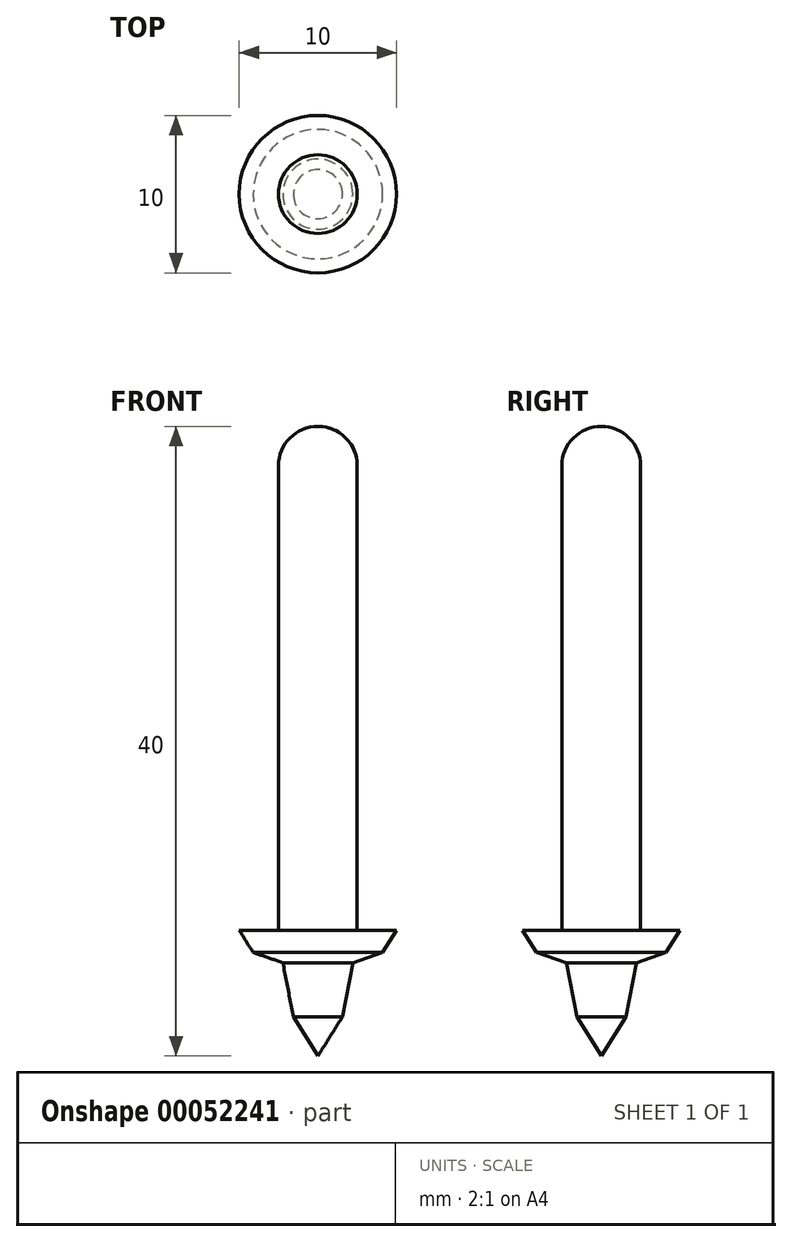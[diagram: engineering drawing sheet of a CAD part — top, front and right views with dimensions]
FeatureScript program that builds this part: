
annotation { "Feature Type Name" : "Feature", "Feature Type Description" : "" }
export const myFeature = defineFeature(function(context is Context, id is Id, definition is map)
    precondition{}
    {
        {
            var Q0;
            Q0=qCreatedBy(makeId("Front.planeOp"),FACE);
            var sketch = newSketch(context, id + "F0", { "sketchPlane" : qUnion([Q0])});
            skLineSegment(sketch, "E0", {"start": v(0, 0) * mm, "end": v(0, 40) * mm});
            skLineSegment(sketch, "E1", {"start": v(0, 8) * mm, "end": v(2.5, 8) * mm});
            skLineSegment(sketch, "E2", {"start": v(2.5, 8) * mm, "end": v(2.5, 37.5) * mm});
            skArc(sketch, "E3", {"start": v(2.5, 37.5) * mm, "mid": v(1.77, 39.27) * mm, "end": v(0, 40) * mm});
            skLineSegment(sketch, "E4", {"start": v(2.5, 37.5) * mm, "end": v(0, 37.5) * mm});
            skLineSegment(sketch, "E5", {"start": v(2.5, 8) * mm, "end": v(5, 8) * mm});
            skLineSegment(sketch, "E6", {"start": v(5, 8) * mm, "end": v(0, 0) * mm});
            skLineSegment(sketch, "E7", {"start": v(1.56, 2.5) * mm, "end": v(2.22, 5.93) * mm});
            skLineSegment(sketch, "E8", {"start": v(2.22, 5.93) * mm, "end": v(4.11, 6.58) * mm});
            skSolve(sketch);
        }
        {
            var Q0;
            {var subQ0=sQuery(id+"F0.wireOp",EDGE,"E1");Q0=makeQuery(id+"F0.imprint","IMPRINT",FACE,{"disambiguationData":[TD([[makeQuery(id+"F0.imprint","IMPRINT",EDGE,{"derivedFrom":subQ0}),1.0]])]});}
            var Q1;
            {var subQ0=sQuery(id+"F0.wireOp",EDGE,"E3");Q1=makeQuery(id+"F0.imprint","IMPRINT",FACE,{"disambiguationData":[TD([[makeQuery(id+"F0.imprint","IMPRINT",EDGE,{"derivedFrom":subQ0}),1.0]])]});}
            var Q2;
            Q2=sQuery(id+"F0.wireOp",EDGE,"E0");
            revolve(context, id + "F1", {"entities" : qUnion([Q0, Q1]), "axis" : qUnion([Q2]), "revolveType" : RevolveType.FULL});
        }
        {
            var Q0;
            {var subQ3=sQuery(id+"F0.wireOp",EDGE,"E1");Q0=makeQuery(id+"F0.imprint","IMPRINT",FACE,{"disambiguationData":[TD([[makeQuery(id+"F0.imprint","IMPRINT",EDGE,{"derivedFrom":subQ3}),-1.0]])]});}
            var Q1;
            Q1=sQuery(id+"F0.wireOp",EDGE,"E0");
            revolve(context, id + "F2", {"entities" : qUnion([Q0]), "axis" : qUnion([Q1]), "revolveType" : RevolveType.FULL});
        }
    });
